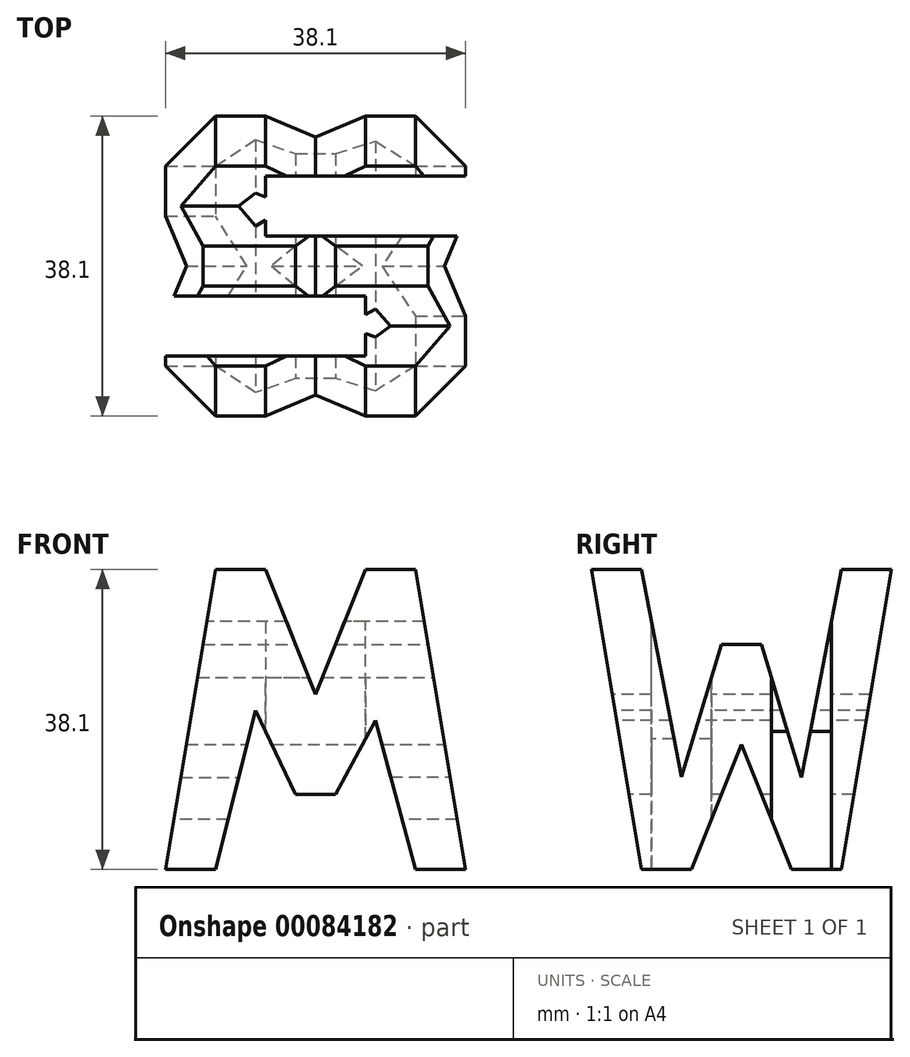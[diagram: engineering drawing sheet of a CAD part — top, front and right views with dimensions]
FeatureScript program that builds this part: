
annotation { "Feature Type Name" : "Feature", "Feature Type Description" : "" }
export const myFeature = defineFeature(function(context is Context, id is Id, definition is map)
    precondition{}
    {
        {
            var Q0;
            Q0=qCreatedBy(makeId("Front.planeOp"),FACE);
            var sketch = newSketch(context, id + "F0", { "sketchPlane" : qUnion([Q0])});
            skLineSegment(sketch, "E0", {"start": v(0, 0) * mm, "end": v(38.1, 0) * mm});
            skLineSegment(sketch, "E1", {"start": v(38.1, 0) * mm, "end": v(38.1, 38.1) * mm});
            skLineSegment(sketch, "E2", {"start": v(38.1, 38.1) * mm, "end": v(0, 38.1) * mm});
            skLineSegment(sketch, "E3", {"start": v(0, 38.1) * mm, "end": v(0, 0) * mm});
            skSolve(sketch);
        }
        {
            var Q0;
            Q0 = qSketchRegion(id + "F0", true);
            extrude(context, id + "F1", {"entities" : qUnion([Q0]), "depth" : 38.1 * mm});
        }
        {
            var Q0;
            Q0=qCreatedBy(makeId("Front.planeOp"),FACE);
            cPlane(context, id + "F2", {"entities" : qUnion([Q0]), "cplaneType" : CPlaneType.OFFSET, "offset" : 38.1 * mm, "width" : 152.4 * mm, "height" : 152.4 * mm});
        }
        {
            var Q0;
            Q0=qCreatedBy(makeId("Right.planeOp"),FACE);
            cPlane(context, id + "F3", {"entities" : qUnion([Q0]), "cplaneType" : CPlaneType.OFFSET, "offset" : 38.1 * mm, "width" : 152.4 * mm, "height" : 152.4 * mm});
        }
        {
            var Q0;
            Q0=qCreatedBy(makeId("Top.planeOp"),FACE);
            cPlane(context, id + "F4", {"entities" : qUnion([Q0]), "cplaneType" : CPlaneType.OFFSET, "offset" : 38.1 * mm, "width" : 152.4 * mm, "height" : 152.4 * mm});
        }
        {
            var Q0;
            Q0=qCreatedBy(id+"F3.planeOp",FACE);
            var sketch = newSketch(context, id + "F5", { "sketchPlane" : qUnion([Q0])});
            skLineSegment(sketch, "E4", {"start": v(0, 0) * mm, "end": v(0, 38.1) * mm});
            skLineSegment(sketch, "E5", {"start": v(0, 38.1) * mm, "end": v(-38.1, 38.1) * mm});
            skLineSegment(sketch, "E6", {"start": v(-38.1, 38.1) * mm, "end": v(-38.1, 0) * mm});
            skLineSegment(sketch, "E7", {"start": v(-38.1, 0) * mm, "end": v(0, 0) * mm});
            skLineSegment(sketch, "E8", {"start": v(-38.1, 38.1) * mm, "end": v(-31.75, 0) * mm});
            skLineSegment(sketch, "E9", {"start": v(-31.75, 0) * mm, "end": v(-25.4, 0) * mm});
            skLineSegment(sketch, "E10", {"start": v(-25.4, 0) * mm, "end": v(-19.05, 15.88) * mm});
            skLineSegment(sketch, "E11", {"start": v(-19.05, 15.88) * mm, "end": v(-12.7, 0) * mm});
            skLineSegment(sketch, "E12", {"start": v(-12.7, 0) * mm, "end": v(-6.35, 0) * mm});
            skLineSegment(sketch, "E13", {"start": v(-6.35, 0) * mm, "end": v(0, 38.1) * mm});
            skLineSegment(sketch, "E14", {"start": v(-6.35, 38.1) * mm, "end": v(-11.43, 11.71) * mm});
            skLineSegment(sketch, "E15", {"start": v(-11.43, 11.71) * mm, "end": v(-16.5, 28.58) * mm});
            skLineSegment(sketch, "E16", {"start": v(-16.5, 28.58) * mm, "end": v(-21.59, 28.58) * mm});
            skLineSegment(sketch, "E17", {"start": v(-21.59, 28.58) * mm, "end": v(-26.67, 11.75) * mm});
            skLineSegment(sketch, "E18", {"start": v(-26.67, 11.75) * mm, "end": v(-31.75, 38.1) * mm});
            skLineSegment(sketch, "E19", {"start": v(-31.75, 38.1) * mm, "end": v(-38.1, 38.1) * mm});
            skSolve(sketch);
        }
        {
            var Q0;
            {var subQ0=sQuery(id+"F5.wireOp",EDGE,"E6");Q0=makeQuery(id+"F5.imprint","IMPRINT",FACE,{"disambiguationData":[TD([[makeQuery(id+"F5.imprint","IMPRINT",EDGE,{"derivedFrom":subQ0}),1.0]])]});}
            var Q1;
            {var subQ0=sQuery(id+"F5.wireOp",EDGE,"E14");Q1=makeQuery(id+"F5.imprint","IMPRINT",FACE,{"disambiguationData":[TD([[makeQuery(id+"F5.imprint","IMPRINT",EDGE,{"derivedFrom":subQ0}),-1.0]])]});}
            var Q2;
            {var subQ0=sQuery(id+"F5.wireOp",EDGE,"E10");Q2=makeQuery(id+"F5.imprint","IMPRINT",FACE,{"disambiguationData":[TD([[makeQuery(id+"F5.imprint","IMPRINT",EDGE,{"derivedFrom":subQ0}),-1.0]])]});}
            var Q3;
            {var subQ0=sQuery(id+"F5.wireOp",EDGE,"E4");Q3=makeQuery(id+"F5.imprint","IMPRINT",FACE,{"disambiguationData":[TD([[makeQuery(id+"F5.imprint","IMPRINT",EDGE,{"derivedFrom":subQ0}),1.0]])]});}
            extrude(context, id + "F6", {"entities" : qUnion([Q0, Q1, Q2, Q3]), "operationType" : NewBodyOperationType.REMOVE, "oppositeDirection" : true, "depth" : 38.1 * mm});
        }
        {
            var Q0;
            Q0=qCreatedBy(id+"F2.planeOp",FACE);
            var sketch = newSketch(context, id + "F7", { "sketchPlane" : qUnion([Q0])});
            skLineSegment(sketch, "E20", {"start": v(0, 0) * mm, "end": v(0, 38.1) * mm});
            skLineSegment(sketch, "E21", {"start": v(0, 38.1) * mm, "end": v(38.1, 38.1) * mm});
            skLineSegment(sketch, "E22", {"start": v(38.1, 38.1) * mm, "end": v(38.1, 0) * mm});
            skLineSegment(sketch, "E23", {"start": v(38.1, 0) * mm, "end": v(0, 0) * mm});
            skLineSegment(sketch, "E24", {"start": v(0, 0) * mm, "end": v(6.35, 38.1) * mm});
            skLineSegment(sketch, "E25", {"start": v(6.35, 38.1) * mm, "end": v(12.7, 38.1) * mm});
            skLineSegment(sketch, "E26", {"start": v(12.7, 38.1) * mm, "end": v(19.05, 22.23) * mm});
            skLineSegment(sketch, "E27", {"start": v(19.05, 22.22) * mm, "end": v(25.4, 38.1) * mm});
            skLineSegment(sketch, "E28", {"start": v(25.4, 38.1) * mm, "end": v(31.75, 38.1) * mm});
            skLineSegment(sketch, "E29", {"start": v(31.75, 38.1) * mm, "end": v(38.1, 0) * mm});
            skLineSegment(sketch, "E30", {"start": v(31.75, 0) * mm, "end": v(26.67, 18.94) * mm});
            skLineSegment(sketch, "E31", {"start": v(26.67, 18.94) * mm, "end": v(21.59, 9.52) * mm});
            skLineSegment(sketch, "E32", {"start": v(21.6, 9.53) * mm, "end": v(16.51, 9.53) * mm});
            skLineSegment(sketch, "E33", {"start": v(16.51, 9.53) * mm, "end": v(11.43, 20.19) * mm});
            skLineSegment(sketch, "E34", {"start": v(11.43, 20.19) * mm, "end": v(6.35, 0) * mm});
            skLineSegment(sketch, "E35", {"start": v(6.35, 0) * mm, "end": v(0, 0) * mm});
            skSolve(sketch);
        }
        {
            var Q0;
            {var subQ0=sQuery(id+"F7.wireOp",EDGE,"E20");Q0=makeQuery(id+"F7.imprint","IMPRINT",FACE,{"disambiguationData":[TD([[makeQuery(id+"F7.imprint","IMPRINT",EDGE,{"derivedFrom":subQ0}),-1.0]])]});}
            var Q1;
            {var subQ0=sQuery(id+"F7.wireOp",EDGE,"E26");Q1=makeQuery(id+"F7.imprint","IMPRINT",FACE,{"disambiguationData":[TD([[makeQuery(id+"F7.imprint","IMPRINT",EDGE,{"derivedFrom":subQ0}),1.0]])]});}
            var Q2;
            {var subQ0=sQuery(id+"F7.wireOp",EDGE,"E22");Q2=makeQuery(id+"F7.imprint","IMPRINT",FACE,{"disambiguationData":[TD([[makeQuery(id+"F7.imprint","IMPRINT",EDGE,{"derivedFrom":subQ0}),-1.0]])]});}
            var Q3;
            {var subQ0=sQuery(id+"F7.wireOp",EDGE,"E30");Q3=makeQuery(id+"F7.imprint","IMPRINT",FACE,{"disambiguationData":[TD([[makeQuery(id+"F7.imprint","IMPRINT",EDGE,{"derivedFrom":subQ0}),1.0]])]});}
            extrude(context, id + "F8", {"entities" : qUnion([Q0, Q1, Q2, Q3]), "operationType" : NewBodyOperationType.REMOVE, "oppositeDirection" : true, "depth" : 38.1 * mm});
        }
        {
            var Q0;
            Q0=qCreatedBy(id+"F4.planeOp",FACE);
            var sketch = newSketch(context, id + "F9", { "sketchPlane" : qUnion([Q0])});
            skLineSegment(sketch, "E36", {"start": v(0, 0) * mm, "end": v(38.1, 0) * mm});
            skLineSegment(sketch, "E37", {"start": v(38.1, 0) * mm, "end": v(38.1, -38.1) * mm});
            skLineSegment(sketch, "E38", {"start": v(38.1, -38.1) * mm, "end": v(0, -38.1) * mm});
            skLineSegment(sketch, "E39", {"start": v(0, -38.1) * mm, "end": v(0, 0) * mm});
            skLineSegment(sketch, "E40", {"start": v(38.1, -7.62) * mm, "end": v(12.7, -7.62) * mm});
            skLineSegment(sketch, "E41", {"start": v(12.7, -7.62) * mm, "end": v(12.7, -15.24) * mm});
            skLineSegment(sketch, "E42", {"start": v(12.7, -15.24) * mm, "end": v(38.1, -15.24) * mm});
            skLineSegment(sketch, "E43", {"start": v(38.1, -15.24) * mm, "end": v(38.1, -7.62) * mm});
            skLineSegment(sketch, "E44", {"start": v(0, -22.86) * mm, "end": v(25.4, -22.86) * mm});
            skLineSegment(sketch, "E45", {"start": v(25.4, -22.86) * mm, "end": v(25.4, -30.48) * mm});
            skLineSegment(sketch, "E46", {"start": v(25.4, -30.48) * mm, "end": v(0, -30.48) * mm});
            skLineSegment(sketch, "E47", {"start": v(0, -30.48) * mm, "end": v(0, -22.86) * mm});
            skSolve(sketch);
        }
        {
            var Q0;
            Q0=makeQuery(id+"F9.imprint","IMPRINT",FACE,{"disambiguationData":[TD([[makeQuery(id+"F9.imprint","IMPRINT",EDGE,{"derivedFrom":sQuery(id+"F9.wireOp",EDGE,"E40")}),1.0]])]});
            var Q1;
            Q1=makeQuery(id+"F9.imprint","IMPRINT",FACE,{"disambiguationData":[TD([[makeQuery(id+"F9.imprint","IMPRINT",EDGE,{"derivedFrom":sQuery(id+"F9.wireOp",EDGE,"E44")}),-1.0]])]});
            extrude(context, id + "F10", {"entities" : qUnion([Q0, Q1]), "operationType" : NewBodyOperationType.REMOVE, "oppositeDirection" : true, "depth" : 38.1 * mm});
        }
    });
